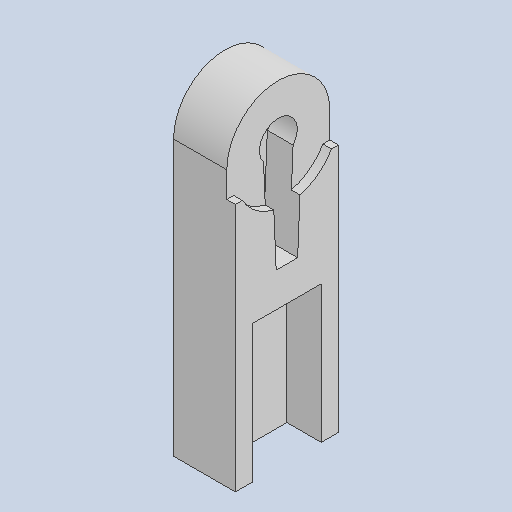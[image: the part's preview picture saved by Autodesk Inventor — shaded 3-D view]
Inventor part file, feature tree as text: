
AUTODESK INVENTOR PART (.ipt)
format: ipt  version: 2023 (Build 270158000, 158)  size: 122,880 bytes
history: native  units: in
note: dims shown in document units (in); Inventor stores cm internally (conversion verified against a paired STEP export)
features: sketch x4, other x3
ambient origin geometry x8: Origin, YZ Plane, XZ Plane, XY Plane, X Axis, Y Axis, Z Axis, Center Point
bodies: Solid1 (feature_tree)
feature tree (7):
  other  "Part_3_hand.ipt"
  other  "Solid1::Part_3_hand.ipt"
  other  "TaggingFeature1"
  sketch  "Sketch1"  dims[d0=0.3937in]
  sketch  "Sketch2"
  sketch  "Sketch3"
  sketch  "Sketch4"
